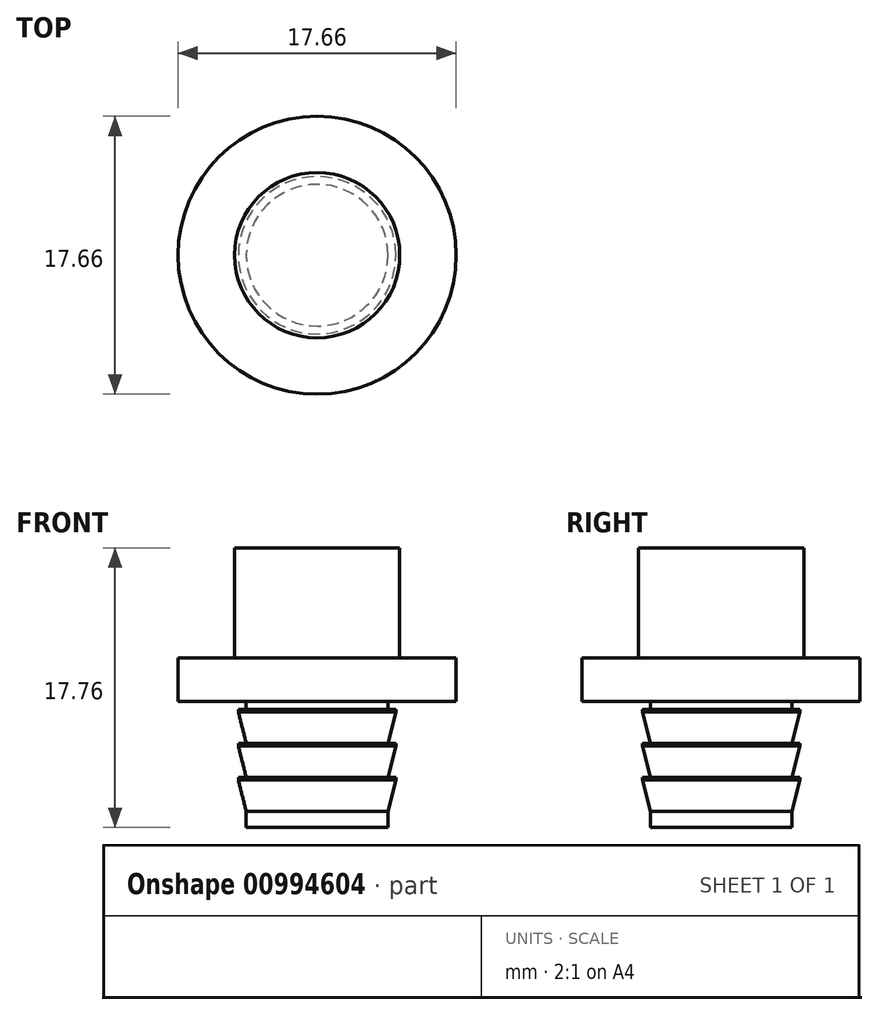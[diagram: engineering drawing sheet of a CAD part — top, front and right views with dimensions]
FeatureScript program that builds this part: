
annotation { "Feature Type Name" : "Feature", "Feature Type Description" : "" }
export const myFeature = defineFeature(function(context is Context, id is Id, definition is map)
    precondition{}
    {
        {
            var Q0;
            Q0=qCreatedBy(makeId("Top.planeOp"),FACE);
            var sketch = newSketch(context, id + "F0", { "sketchPlane" : qUnion([Q0])});
            skCircle(sketch, "E0", {"center": v(0, 0) * mm, "radius": 8.83 * mm});
            skSolve(sketch);
        }
        {
            var Q0;
            Q0=makeQuery(id+"F0.imprint","IMPRINT",FACE,{"disambiguationData":[TD([[makeQuery(id+"F0.imprint","IMPRINT",EDGE,{"derivedFrom":sQuery(id+"F0.wireOp",EDGE,"E0")}),1.0]])]});
            extrude(context, id + "F1", {"entities" : qUnion([Q0]), "depth" : 2.76 * mm, "offsetDistance" : 25 * mm});
        }
        {
            var Q0;
            Q0=qCreatedBy(makeId("Right.planeOp"),FACE);
            var sketch = newSketch(context, id + "F2", { "sketchPlane" : qUnion([Q0])});
            skLineSegment(sketch, "E1", {"start": v(0, 0) * mm, "end": v(-4.5, 0) * mm});
            skLineSegment(sketch, "E2", {"start": v(-4.5, 0) * mm, "end": v(-4.5, -0.5) * mm});
            skLineSegment(sketch, "E3", {"start": v(-4.5, -0.5) * mm, "end": v(-5, -0.5) * mm});
            skLineSegment(sketch, "E4", {"start": v(-5, -0.5) * mm, "end": v(-5, -0.67) * mm});
            skLineSegment(sketch, "E5", {"start": v(-5, -0.67) * mm, "end": v(-4.5, -2.67) * mm});
            skLineSegment(sketch, "E6", {"start": v(-4.5, -2.67) * mm, "end": v(-4.5, -2.67) * mm});
            skLineSegment(sketch, "E7", {"start": v(-4.5, -2.67) * mm, "end": v(-5, -2.67) * mm});
            skLineSegment(sketch, "E8", {"start": v(-5, -2.67) * mm, "end": v(-5, -2.83) * mm});
            skLineSegment(sketch, "E9", {"start": v(-5, -2.83) * mm, "end": v(-4.5, -4.83) * mm});
            skLineSegment(sketch, "E10", {"start": v(-4.5, -4.83) * mm, "end": v(-4.5, -4.83) * mm});
            skLineSegment(sketch, "E11", {"start": v(-4.5, -4.83) * mm, "end": v(-5, -4.83) * mm});
            skLineSegment(sketch, "E12", {"start": v(-5, -4.83) * mm, "end": v(-5, -5) * mm});
            skLineSegment(sketch, "E13", {"start": v(-5, -5) * mm, "end": v(-4.5, -7) * mm});
            skLineSegment(sketch, "E14", {"start": v(-4.5, -7) * mm, "end": v(-4.5, -8) * mm});
            skLineSegment(sketch, "E15", {"start": v(-4.5, -8) * mm, "end": v(0, -8) * mm});
            skLineSegment(sketch, "E16", {"start": v(0, -8) * mm, "end": v(0, 0) * mm});
            skSolve(sketch);
        }
        {
            var Q0;
            Q0=makeQuery(id+"F2.imprint","IMPRINT",FACE,{"disambiguationData":[TD([[makeQuery(id+"F2.imprint","IMPRINT",EDGE,{"derivedFrom":sQuery(id+"F2.wireOp",EDGE,"E1")}),1.0]])]});
            var Q1;
            Q1=sQuery(id+"F2.wireOp",EDGE,"E16");
            revolve(context, id + "F3", {"operationType" : NewBodyOperationType.ADD, "surfaceOperationType" : NewSurfaceOperationType.NEW, "entities" : qUnion([Q0]), "axis" : qUnion([Q1]), "revolveType" : RevolveType.FULL});
        }
        {
            var Q0;
            Q0=makeQuery(id+"F1.opExtrude","CAP_FACE",FACE,{"disambiguationData":[OSD([sQuery(id+"F0.wireOp",EDGE,"E0")])],"isStart":false});
            var sketch = newSketch(context, id + "F4", { "sketchPlane" : qUnion([Q0])});
            skCircle(sketch, "E17", {"center": v(0, 0) * mm, "radius": 5.25 * mm});
            skSolve(sketch);
        }
        {
            var Q0;
            Q0 = qSketchRegion(id + "F4", true);
            extrude(context, id + "F5", {"entities" : qUnion([Q0]), "operationType" : NewBodyOperationType.ADD, "depth" : 7 * mm, "offsetDistance" : 25 * mm});
        }
    });
